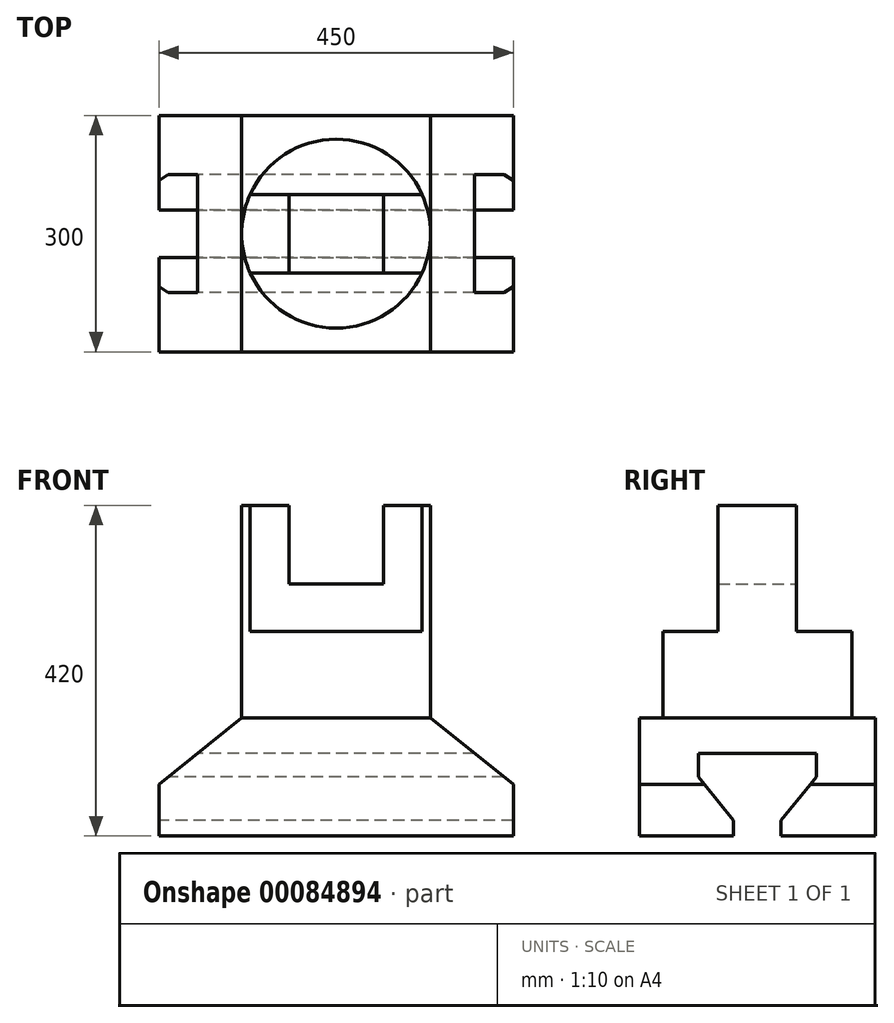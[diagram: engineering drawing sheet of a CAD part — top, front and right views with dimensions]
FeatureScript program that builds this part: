
annotation { "Feature Type Name" : "Feature", "Feature Type Description" : "" }
export const myFeature = defineFeature(function(context is Context, id is Id, definition is map)
    precondition{}
    {
        {
            var Q0;
            Q0=qCreatedBy(makeId("Front.planeOp"),FACE);
            var sketch = newSketch(context, id + "F0", { "sketchPlane" : qUnion([Q0])});
            skLineSegment(sketch, "E0.bottom", {"start": v(-225, -75) * mm, "end": v(225, -75) * mm});
            skLineSegment(sketch, "E0.top", {"start": v(-120, 75) * mm, "end": v(120, 75) * mm});
            skLineSegment(sketch, "E0.left", {"start": v(-225, -75) * mm, "end": v(-225, -9.42) * mm});
            skLineSegment(sketch, "E0.right", {"start": v(225, -75) * mm, "end": v(225, -9.42) * mm});
            skPoint(sketch, "E0.middle", {"position": v(0, 0) * mm});
            skLineSegment(sketch, "E1", {"start": v(-120, 75) * mm, "end": v(-225, -9.42) * mm});
            skLineSegment(sketch, "E2", {"start": v(120, 75) * mm, "end": v(225, -9.42) * mm});
            skPoint(sketch, "E3.orphan", {"position": v(225, 75) * mm});
            skPoint(sketch, "E4.orphan", {"position": v(-225, 75) * mm});
            skSolve(sketch);
        }
        {
            var Q0;
            Q0 = qSketchRegion(id + "F0", true);
            extrude(context, id + "F1", {"entities" : qUnion([Q0]), "depth" : 300 * mm});
        }
        {
            var Q0;
            Q0=makeQuery(id+"F1.opExtrude","SWEPT_FACE",FACE,{"disambiguationData":[OSD([sQuery(id+"F0.wireOp",EDGE,"E0.top")])]});
            var sketch = newSketch(context, id + "F2", { "sketchPlane" : qUnion([Q0])});
            skCircle(sketch, "E5", {"center": v(0, -150) * mm, "radius": 120 * mm});
            skPoint(sketch, "E5.centerSnap0", {"position": v(120, -150) * mm});
            skSolve(sketch);
        }
        {
            var Q0;
            Q0 = qSketchRegion(id + "F2", true);
            extrude(context, id + "F3", {"entities" : qUnion([Q0]), "operationType" : NewBodyOperationType.ADD, "depth" : 270 * mm});
        }
        {
            var Q0;
            Q0=makeQuery(id+"F3.opExtrude","CAP_FACE",FACE,{"disambiguationData":[OSD([sQuery(id+"F2.wireOp",EDGE,"E5")])],"isStart":false});
            var sketch = newSketch(context, id + "F4", { "sketchPlane" : qUnion([Q0])});
            skLineSegment(sketch, "E6.bottom", {"start": v(-154.1, -100) * mm, "end": v(154.1, -100) * mm});
            skLineSegment(sketch, "E6.top", {"start": v(-154.1, -200) * mm, "end": v(154.1, -200) * mm});
            skPoint(sketch, "E6.middle", {"position": v(0, -150) * mm});
            skLineSegment(sketch, "E7", {"start": v(-154.1, -100) * mm, "end": v(-154.1, -14.9) * mm});
            skLineSegment(sketch, "E8", {"start": v(-154.1, -14.9) * mm, "end": v(154.1, -14.9) * mm});
            skLineSegment(sketch, "E9", {"start": v(154.1, -14.9) * mm, "end": v(154.1, -100) * mm});
            skLineSegment(sketch, "E10", {"start": v(154.1, -200) * mm, "end": v(154.1, -271.97) * mm});
            skLineSegment(sketch, "E11", {"start": v(154.1, -271.97) * mm, "end": v(-154.1, -271.97) * mm});
            skLineSegment(sketch, "E12", {"start": v(-154.1, -271.97) * mm, "end": v(-154.1, -200) * mm});
            skSolve(sketch);
        }
        {
            var Q0;
            Q0 = qSketchRegion(id + "F4", true);
            extrude(context, id + "F5", {"entities" : qUnion([Q0]), "operationType" : NewBodyOperationType.REMOVE, "oppositeDirection" : true, "depth" : 160 * mm});
        }
        {
            var Q0;
            Q0=makeQuery(id+"F3.opExtrude","CAP_FACE",FACE,{"disambiguationData":[OSD([sQuery(id+"F2.wireOp",EDGE,"E5")])],"isStart":false});
            var sketch = newSketch(context, id + "F6", { "sketchPlane" : qUnion([Q0])});
            skLineSegment(sketch, "E13.bottom", {"start": v(-60, -200) * mm, "end": v(60, -200) * mm});
            skLineSegment(sketch, "E13.top", {"start": v(-60, -100) * mm, "end": v(60, -100) * mm});
            skLineSegment(sketch, "E13.left", {"start": v(-60, -200) * mm, "end": v(-60, -100) * mm});
            skLineSegment(sketch, "E13.right", {"start": v(60, -200) * mm, "end": v(60, -100) * mm});
            skPoint(sketch, "E13.middle", {"position": v(0, -150) * mm});
            skSolve(sketch);
        }
        {
            var Q0;
            Q0 = qSketchRegion(id + "F6", true);
            extrude(context, id + "F7", {"entities" : qUnion([Q0]), "operationType" : NewBodyOperationType.REMOVE, "oppositeDirection" : true, "depth" : 100 * mm});
        }
        {
            var Q0;
            Q0=makeQuery(id+"F1.opExtrude","SWEPT_FACE",FACE,{"disambiguationData":[OSD([sQuery(id+"F0.wireOp",EDGE,"E0.left")])]});
            var sketch = newSketch(context, id + "F8", { "sketchPlane" : qUnion([Q0])});
            skLineSegment(sketch, "E14.bottom", {"start": v(120, -95) * mm, "end": v(180, -95) * mm});
            skLineSegment(sketch, "E14.top", {"start": v(120, -55) * mm, "end": v(180, -55) * mm});
            skLineSegment(sketch, "E14.left", {"start": v(120, -95) * mm, "end": v(120, -55) * mm});
            skLineSegment(sketch, "E14.right", {"start": v(180, -95) * mm, "end": v(180, -55) * mm});
            skPoint(sketch, "E14.middle", {"position": v(150, -75) * mm});
            skLineSegment(sketch, "E15", {"start": v(180, -55) * mm, "end": v(225, 0) * mm});
            skLineSegment(sketch, "E16", {"start": v(225, 0) * mm, "end": v(225, 30) * mm});
            skLineSegment(sketch, "E17", {"start": v(225, 30) * mm, "end": v(75, 30) * mm});
            skLineSegment(sketch, "E18", {"start": v(75, 30) * mm, "end": v(75, 0) * mm});
            skLineSegment(sketch, "E19", {"start": v(75, 0) * mm, "end": v(120, -55) * mm});
            skPoint(sketch, "E20", {"position": v(150, 30) * mm});
            skSolve(sketch);
        }
        {
            var Q0;
            Q0 = qSketchRegion(id + "F8", true);
            extrude(context, id + "F9", {"entities" : qUnion([Q0]), "operationType" : NewBodyOperationType.REMOVE, "endBound" : BoundingType.THROUGH_ALL, "oppositeDirection" : true, "depth" : 25 * mm});
        }
    });
